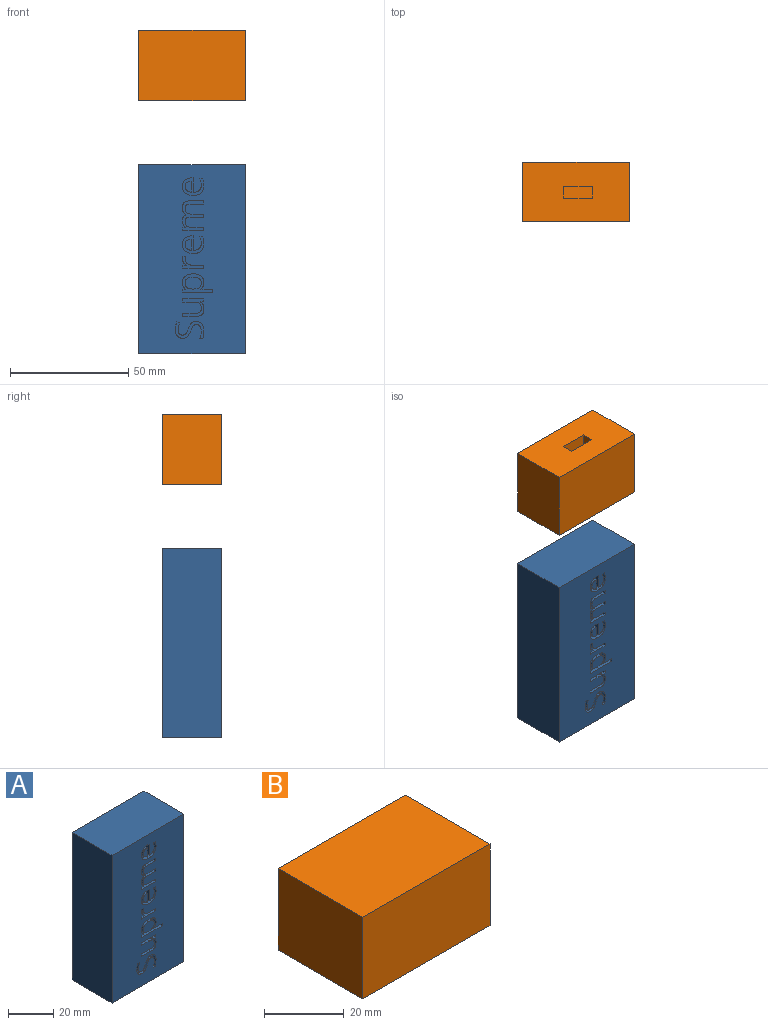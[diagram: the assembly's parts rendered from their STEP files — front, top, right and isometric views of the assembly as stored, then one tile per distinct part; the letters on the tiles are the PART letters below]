
ASSEMBLY  parts=2 mates=1
PART A: 167 faces, bbox 45x25x80 mm
  f0: plane 45x25mm, normal (0,0,-1), area 1065mm2, adj f1,f2,f3,f5,f162,f163,f164,f165
  f1: plane 80x45mm, normal (0,-1,0), area 3330.5mm2, adj f0,f2,f3,f4,f14,f15,f16,f17
  f2: plane 80x25mm, normal (-1,0,0), area 2000mm2, adj f0,f1,f4,f5
  f3: plane 80x25mm, normal (1,0,0), area 2000mm2, adj f0,f1,f4,f5
  f4: plane 45x25mm, normal (0,0,1), area 1125mm2, adj f1,f2,f3,f5
  f5: plane 80x45mm, normal (0,1,0), area 3600mm2, adj f0,f2,f3,f4
  f6: extruded ~2x1.96mm, area 4.3mm2, adj f7,f30,f31,f159
  f7: extruded ~2x1.82mm, area 4.2mm2, adj f6,f8,f31,f159
  f8: extruded ~2.53x2mm, area 5.3mm2, adj f7,f9,f31,f159
  f9: extruded ~2.55x2mm, area 5.3mm2, adj f8,f10,f31,f159
  f10: extruded ~2x1.79mm, area 4.2mm2, adj f9,f11,f31,f159
  f11: extruded ~2x1.99mm, area 4.4mm2, adj f10,f12,f31,f159
  f12: extruded ~2.66x2mm, area 5.6mm2, adj f11,f13,f31,f159
  f13: plane 2x0.3mm, normal (0,0,-1), area 0.6mm2, adj f12,f30,f31,f159
  f14: extruded ~2x1.57mm, area 3.2mm2, adj f1,f15,f29,f31
  f15: extruded ~2.69x2mm, area 6.1mm2, adj f1,f14,f16,f31
  f16: extruded ~3.38x2mm, area 7.2mm2, adj f1,f15,f17,f31
  f17: extruded ~3.36x2mm, area 7.1mm2, adj f1,f16,f18,f31
  f18: extruded ~2.71x2mm, area 6.1mm2, adj f1,f17,f19,f31
  f19: extruded ~2x1.57mm, area 3.2mm2, adj f1,f18,f20,f31
  f20: extruded ~2x1.2mm, area 3.2mm2, adj f1,f19,f21,f31
  f21: plane 2x0.06mm, normal (1,0,0), area 0.1mm2, adj f1,f20,f22,f31
  f22: plane 2x1.21mm, normal (0.15,0,-0.99), area 2.4mm2, adj f1,f21,f23,f31
  f23: plane 2x1.09mm, normal (1,0,0), area 2.2mm2, adj f1,f22,f24,f31
  f24: plane 12.78x2mm, normal (0,0,1), area 25.6mm2, adj f1,f23,f25,f31
  f25: plane 2x1.34mm, normal (-1,0,0), area 2.7mm2, adj f1,f24,f26,f31
  f26: plane 3.63x2mm, normal (0,0,-1), area 7.3mm2, adj f1,f25,f27,f31
  f27: extruded ~2x1.47mm, area 2.9mm2, adj f1,f26,f28,f31
  f28: plane 2x0.1mm, normal (-1,0,0), area 0.2mm2, adj f1,f27,f29,f31
  f29: extruded ~2x1.19mm, area 3.1mm2, adj f1,f14,f28,f31
  f30: extruded ~2.38x2mm, area 5mm2, adj f6,f13,f31,f159
  f31: plane 12.94x7.76mm, normal (0,-1,0), area 38.5mm2, adj f6,f7,f8,f9,f10,f11,f12,f13
  f32: plane 5.74x2mm, normal (0,0,1), area 11.5mm2, adj f1,f33,f59,f60
  f33: plane 2x1.33mm, normal (-1,0,0), area 2.7mm2, adj f1,f32,f34,f60
  f34: plane 5.75x2mm, normal (0,0,-1), area 11.5mm2, adj f1,f33,f35,f60
  f35: extruded ~2.46x2mm, area 5.3mm2, adj f1,f34,f36,f60
  f36: extruded ~2.24x2mm, area 4.9mm2, adj f1,f35,f37,f60
  f37: extruded ~2x1.71mm, area 3.5mm2, adj f1,f36,f38,f60
  f38: extruded ~2x1.14mm, area 3.2mm2, adj f1,f37,f39,f60
  f39: plane 2x0.06mm, normal (1,0,0), area 0.1mm2, adj f1,f38,f40,f60
  f40: extruded ~2.7x2mm, area 6.6mm2, adj f1,f39,f41,f60
  f41: extruded ~2x1.54mm, area 3.2mm2, adj f1,f40,f42,f60
  f42: extruded ~2x1.07mm, area 3mm2, adj f1,f41,f43,f60
  f43: plane 2x0.06mm, normal (1,0,0), area 0.1mm2, adj f1,f42,f44,f60
  f44: plane 2x1.21mm, normal (0.18,0,-0.98), area 2.5mm2, adj f1,f43,f45,f60
  f45: plane 2x1.09mm, normal (1,0,0), area 2.2mm2, adj f1,f44,f46,f60
  f46: plane 8.82x2mm, normal (0,0,1), area 17.6mm2, adj f1,f45,f47,f60
  f47: plane 2x1.34mm, normal (-1,0,0), area 2.7mm2, adj f1,f46,f48,f60
  f48: plane 4.63x2mm, normal (0,0,-1), area 9.3mm2, adj f1,f47,f49,f60
  f49: extruded ~2.47x2mm, area 5.2mm2, adj f1,f48,f50,f60
  f50: extruded ~2x1.84mm, area 4.1mm2, adj f1,f49,f51,f60
  f51: extruded ~2x1.41mm, area 3.1mm2, adj f1,f50,f52,f60
  f52: extruded ~2x1.58mm, area 3.4mm2, adj f1,f51,f53,f60
  f53: plane 5.74x2mm, normal (0,0,1), area 11.5mm2, adj f1,f52,f54,f60
  f54: plane 2x1.34mm, normal (-1,0,0), area 2.7mm2, adj f1,f53,f55,f60
  f55: plane 4.92x2mm, normal (0,0,-1), area 9.8mm2, adj f1,f54,f56,f60
  f56: extruded ~2.2x2mm, area 4.7mm2, adj f1,f55,f57,f60
  f57: extruded ~2x1.84mm, area 4.1mm2, adj f1,f56,f58,f60
  f58: extruded ~2x1.4mm, area 3.1mm2, adj f1,f57,f59,f60
  f59: extruded ~2x1.58mm, area 3.4mm2, adj f1,f32,f58,f60
  f60: plane 12.57x8.98mm, normal (0,-1,0), area 44.1mm2, adj f32,f33,f34,f35,f36,f37,f38,f39
  f61: extruded ~2x1.05mm, area 2.1mm2, adj f1,f62,f73,f74
  f62: extruded ~2x1.52mm, area 3.2mm2, adj f1,f61,f63,f74
  f63: extruded ~2x1.33mm, area 3.6mm2, adj f1,f62,f64,f74
  f64: plane 2x0.06mm, normal (1,0,0), area 0.1mm2, adj f1,f63,f65,f74
  f65: plane 2x1.63mm, normal (0.09,0,-1), area 3.3mm2, adj f1,f64,f66,f74
  f66: plane 2x1.1mm, normal (1,0,0), area 2.2mm2, adj f1,f65,f67,f74
  f67: plane 8.82x2mm, normal (0,0,1), area 17.6mm2, adj f1,f66,f68,f74
  f68: plane 2x1.34mm, normal (-1,0,0), area 2.7mm2, adj f1,f67,f69,f74
  f69: plane 4.73x2mm, normal (0,0,-1), area 9.5mm2, adj f1,f68,f70,f74
  f70: extruded ~2.16x2mm, area 4.7mm2, adj f1,f69,f71,f74
  f71: extruded ~2x1.83mm, area 4.2mm2, adj f1,f70,f72,f74
  f72: extruded ~2x0.97mm, area 1.9mm2, adj f1,f71,f73,f74
  f73: plane 2x1.24mm, normal (-0.15,0,-0.99), area 2.5mm2, adj f1,f61,f72,f74
  f74: plane 8.98x5.08mm, normal (0,-1,0), area 16.2mm2, adj f61,f62,f63,f64,f65,f66,f67,f68
  f75: plane 5.72x2mm, normal (0,0,-1), area 11.4mm2, adj f1,f76,f91,f92
  f76: plane 2x1.35mm, normal (1,0,0), area 2.7mm2, adj f1,f75,f77,f92
  f77: plane 5.77x2mm, normal (0,0,1), area 11.5mm2, adj f1,f76,f78,f92
  f78: extruded ~2.45x2mm, area 5.3mm2, adj f1,f77,f79,f92
  f79: extruded ~2.41x2mm, area 5.2mm2, adj f1,f78,f80,f92
  f80: extruded ~2x1.66mm, area 3.4mm2, adj f1,f79,f81,f92
  f81: extruded ~2x1.14mm, area 3.1mm2, adj f1,f80,f82,f92
  f82: plane 2x0.07mm, normal (-1,0,0), area 0.1mm2, adj f1,f81,f83,f92
  f83: plane 2x1.18mm, normal (-0.16,0,0.99), area 2.4mm2, adj f1,f82,f84,f92
  f84: plane 2x1.1mm, normal (-1,0,0), area 2.2mm2, adj f1,f83,f85,f92
  f85: plane 8.82x2mm, normal (0,0,-1), area 17.6mm2, adj f1,f84,f86,f92
  f86: plane 2x1.34mm, normal (1,0,0), area 2.7mm2, adj f1,f85,f87,f92
  f87: plane 4.63x2mm, normal (0,0,1), area 9.3mm2, adj f1,f86,f88,f92
  f88: extruded ~2.47x2mm, area 5.2mm2, adj f1,f87,f89,f92
  f89: extruded ~2.02x2mm, area 4.5mm2, adj f1,f88,f90,f92
  f90: extruded ~2x1.54mm, area 3.3mm2, adj f1,f89,f91,f92
  f91: extruded ~2x1.61mm, area 3.4mm2, adj f1,f75,f90,f92
  f92: plane 8.98x7.38mm, normal (0,-1,0), area 28.3mm2, adj f75,f76,f77,f78,f79,f80,f81,f82
  f93: extruded ~2x1.69mm, area 3.8mm2, adj f94,f111,f112,f160
  f94: extruded ~2x1.61mm, area 3.6mm2, adj f93,f95,f112,f160
  f95: extruded ~2x1.93mm, area 4.1mm2, adj f94,f96,f112,f160
  f96: plane 4.61x2mm, normal (1,0,0), area 9.2mm2, adj f95,f111,f112,f160
  f97: extruded ~3.09x2mm, area 6.8mm2, adj f1,f98,f110,f112
  f98: extruded ~2x1.52mm, area 3.1mm2, adj f1,f97,f99,f112
  f99: extruded ~2x1.34mm, area 2.8mm2, adj f1,f98,f100,f112
  f100: plane 2x1.19mm, normal (0,0,-1), area 2.4mm2, adj f1,f99,f101,f112
  f101: extruded ~2.81x2mm, area 5.8mm2, adj f1,f100,f102,f112
  f102: extruded ~2.1x2mm, area 4.6mm2, adj f1,f101,f103,f112
  f103: extruded ~2.36x2mm, area 5.1mm2, adj f1,f102,f104,f112
  f104: plane 6.07x2mm, normal (-1,0,0), area 12.1mm2, adj f1,f103,f105,f112
  f105: plane 2x0.84mm, normal (0,0,-1), area 1.7mm2, adj f1,f104,f106,f112
  f106: extruded ~2.88x2mm, area 6.2mm2, adj f1,f105,f107,f112
  f107: extruded ~2.62x2mm, area 5.9mm2, adj f1,f106,f108,f112
  f108: extruded ~2.82x2mm, area 6.4mm2, adj f1,f107,f109,f112
  f109: extruded ~3.39x2mm, area 7.2mm2, adj f1,f108,f110,f112
  f110: extruded ~3.31x2mm, area 7.2mm2, adj f1,f97,f109,f112
  f111: extruded ~2x1.91mm, area 4.2mm2, adj f93,f96,f112,f160
  f112: plane 9.14x7.46mm, normal (0,-1,0), area 31mm2, adj f93,f94,f95,f96,f97,f98,f99,f100
  f113: extruded ~2x1.69mm, area 3.8mm2, adj f114,f131,f132,f161
  f114: extruded ~2x1.61mm, area 3.6mm2, adj f113,f115,f132,f161
  f115: extruded ~2x1.93mm, area 4.1mm2, adj f114,f116,f132,f161
  f116: plane 4.61x2mm, normal (1,0,0), area 9.2mm2, adj f115,f131,f132,f161
  f117: extruded ~3.09x2mm, area 6.8mm2, adj f1,f118,f130,f132
  f118: extruded ~2x1.52mm, area 3.1mm2, adj f1,f117,f119,f132
  f119: extruded ~2x1.34mm, area 2.8mm2, adj f1,f118,f120,f132
  f120: plane 2x1.19mm, normal (0,0,-1), area 2.4mm2, adj f1,f119,f121,f132
  f121: extruded ~2.81x2mm, area 5.8mm2, adj f1,f120,f122,f132
  f122: extruded ~2.1x2mm, area 4.6mm2, adj f1,f121,f123,f132
  f123: extruded ~2.36x2mm, area 5.1mm2, adj f1,f122,f124,f132
  f124: plane 6.07x2mm, normal (-1,0,0), area 12.1mm2, adj f1,f123,f125,f132
  f125: plane 2x0.84mm, normal (0,0,-1), area 1.7mm2, adj f1,f124,f126,f132
  f126: extruded ~2.88x2mm, area 6.2mm2, adj f1,f125,f127,f132
  f127: extruded ~2.62x2mm, area 5.9mm2, adj f1,f126,f128,f132
  f128: extruded ~2.82x2mm, area 6.4mm2, adj f1,f127,f129,f132
  f129: extruded ~3.39x2mm, area 7.2mm2, adj f1,f128,f130,f132
  f130: extruded ~3.31x2mm, area 7.2mm2, adj f1,f117,f129,f132
  f131: extruded ~2x1.91mm, area 4.2mm2, adj f113,f116,f132,f161
  f132: plane 9.14x7.46mm, normal (0,-1,0), area 31mm2, adj f113,f114,f115,f116,f117,f118,f119,f120
  f133: extruded ~2.42x2mm, area 5.5mm2, adj f1,f134,f157,f158
  f134: extruded ~2x1.96mm, area 4.3mm2, adj f1,f133,f135,f158
  f135: extruded ~2.55x2mm, area 5.9mm2, adj f1,f134,f136,f158
  f136: extruded ~2x1.64mm, area 3.6mm2, adj f1,f135,f137,f158
  f137: extruded ~2x0.76mm, area 2.1mm2, adj f1,f136,f138,f158
  f138: extruded ~2x1mm, area 2.1mm2, adj f1,f137,f139,f158
  f139: extruded ~2x1.3mm, area 3mm2, adj f1,f138,f140,f158
  f140: extruded ~2x1.7mm, area 3.6mm2, adj f1,f139,f141,f158
  f141: extruded ~2.83x2mm, area 5.8mm2, adj f1,f140,f142,f158
  f142: plane 2x1.19mm, normal (-0.34,0,-0.94), area 2.5mm2, adj f1,f141,f143,f158
  f143: extruded ~3.23x2mm, area 6.6mm2, adj f1,f142,f144,f158
  f144: extruded ~2.7x2mm, area 5.8mm2, adj f1,f143,f145,f158
  f145: extruded ~2.16x2mm, area 5mm2, adj f1,f144,f146,f158
  f146: extruded ~2.1x2mm, area 4.5mm2, adj f1,f145,f147,f158
  f147: extruded ~2.34x2mm, area 5.5mm2, adj f1,f146,f148,f158
  f148: extruded ~2x1.75mm, area 3.8mm2, adj f1,f147,f149,f158
  f149: extruded ~2x0.82mm, area 2.2mm2, adj f1,f148,f150,f158
  f150: extruded ~2x1mm, area 2.1mm2, adj f1,f149,f151,f158
  f151: extruded ~2x1.45mm, area 3.3mm2, adj f1,f150,f152,f158
  f152: extruded ~2.06x2mm, area 4.3mm2, adj f1,f151,f153,f158
  f153: extruded ~2x1.69mm, area 3.4mm2, adj f1,f152,f154,f158
  f154: extruded ~2x1.58mm, area 3.3mm2, adj f1,f153,f155,f158
  f155: plane 2x1.32mm, normal (0,0,1), area 2.6mm2, adj f1,f154,f156,f158
  f156: extruded ~3.22x2mm, area 6.6mm2, adj f1,f155,f157,f158
  f157: extruded ~3.06x2mm, area 6.5mm2, adj f1,f133,f156,f158
  f158: plane 12.09x7.4mm, normal (0,-1,0), area 32mm2, adj f133,f134,f135,f136,f137,f138,f139,f140
  f159: plane 6.89x5.04mm, normal (0,-1,0), area 29.1mm2, adj f6,f7,f8,f9,f10,f11,f12,f13
  f160: plane 4.61x2.61mm, normal (0,-1,0), area 9.7mm2, adj f93,f94,f95,f96,f111
  f161: plane 4.61x2.61mm, normal (0,-1,0), area 9.7mm2, adj f113,f114,f115,f116,f131
  f162: plane 30x15mm, normal (0,1,0), area 450mm2, adj f0,f163,f165,f166
  f163: plane 30x4mm, normal (1,0,0), area 120mm2, adj f0,f162,f164,f166
  f164: plane 30x15mm, normal (0,-1,0), area 450mm2, adj f0,f163,f165,f166
  f165: plane 30x4mm, normal (-1,0,0), area 120mm2, adj f0,f162,f164,f166
  f166: plane 15x4mm, normal (0,0,-1), area 60mm2, adj f162,f163,f164,f165
PART B: 11 faces, bbox 45x30x25 mm
  f0: plane 45x25mm, normal (0,1,0), area 1065mm2, adj f1,f3,f4,f5,f6,f7,f8,f9
  f1: plane 30x25mm, normal (-1,0,0), area 750mm2, adj f0,f2,f4,f5
  f2: plane 45x25mm, normal (0,-1,0), area 1125mm2, adj f1,f3,f4,f5
  f3: plane 30x25mm, normal (1,0,0), area 750mm2, adj f0,f2,f4,f5
  f4: plane 45x30mm, normal (0,0,1), area 1350mm2, adj f0,f1,f2,f3
  f5: plane 45x30mm, normal (0,0,-1), area 1350mm2, adj f0,f1,f2,f3
  f6: plane 15x12mm, normal (0,0,-1), area 180mm2, adj f0,f7,f9,f10
  f7: plane 15x5mm, normal (-1,0,0), area 75mm2, adj f0,f6,f8,f10
  f8: plane 15x12mm, normal (0,0,1), area 180mm2, adj f0,f7,f9,f10
  f9: plane 15x5mm, normal (1,0,0), area 75mm2, adj f0,f6,f8,f10
  f10: plane 12x5mm, normal (0,1,0), area 60mm2, adj f6,f7,f8,f9
PLACE A t=(-37.49,6.54,-15.38)mm
PLACE B rot(axis=(1,0,0),90deg) t=(-59.6,6.54,76.52)mm
MATE slider A.f0 <-> B.f0  axis (0,0,-1) through (-86.19,-18.46,-48.94)mm
